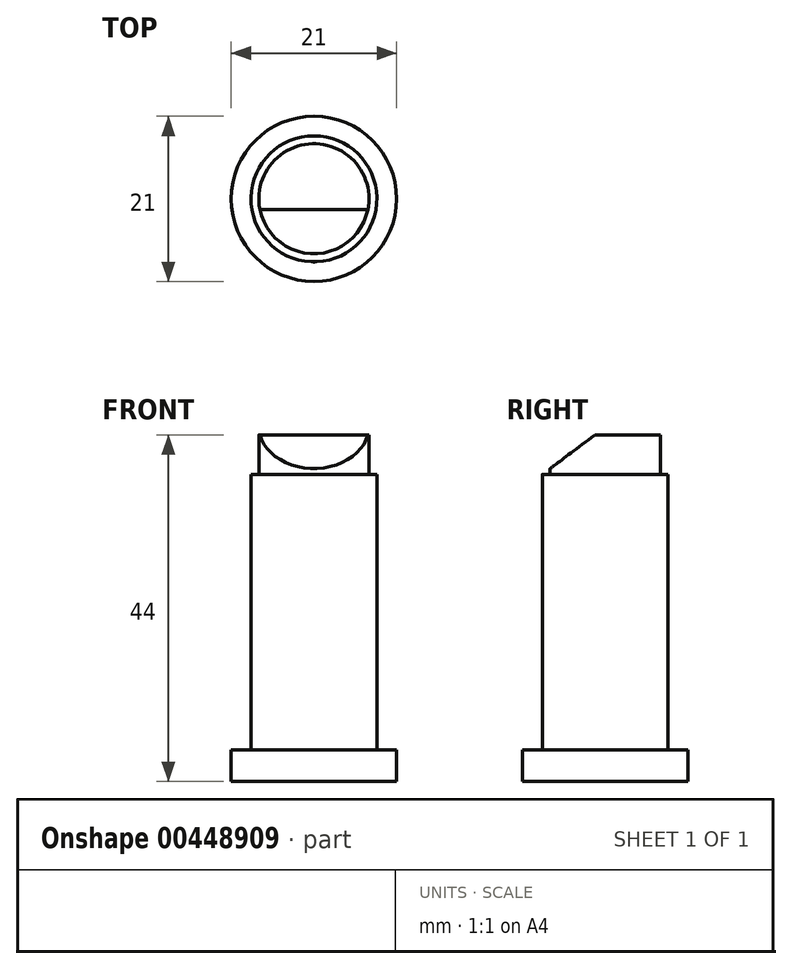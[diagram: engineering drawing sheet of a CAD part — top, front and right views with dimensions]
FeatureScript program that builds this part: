
annotation { "Feature Type Name" : "Feature", "Feature Type Description" : "" }
export const myFeature = defineFeature(function(context is Context, id is Id, definition is map)
    precondition{}
    {
        {
            var Q0;
            Q0=qCreatedBy(makeId("Top.planeOp"),FACE);
            var sketch = newSketch(context, id + "F0", { "sketchPlane" : qUnion([Q0])});
            skCircle(sketch, "E0", {"center": v(0, 0) * mm, "radius": 10.5 * mm});
            skSolve(sketch);
        }
        {
            var Q0;
            Q0=qSketchRegion(id+"F0",true);
            extrude(context, id + "F1", {"entities" : qUnion([Q0]), "depth" : 4 * mm});
        }
        {
            var Q0;
            Q0=qCreatedBy(makeId("Top.planeOp"),FACE);
            var sketch = newSketch(context, id + "F2", { "sketchPlane" : qUnion([Q0])});
            skCircle(sketch, "E1", {"center": v(0, 0) * mm, "radius": 8 * mm});
            skSolve(sketch);
        }
        {
            var Q0;
            Q0=qSketchRegion(id+"F2",true);
            extrude(context, id + "F3", {"entities" : qUnion([Q0]), "operationType" : NewBodyOperationType.ADD, "depth" : 39 * mm});
        }
        {
            var Q0;
            Q0=qCreatedBy(makeId("Right.planeOp"),FACE);
            var sketch = newSketch(context, id + "F4", { "sketchPlane" : qUnion([Q0])});
            skLineSegment(sketch, "E2", {"start": v(0, 44) * mm, "end": v(0, 39) * mm});
            skLineSegment(sketch, "E3", {"start": v(0, 39) * mm, "end": v(7, 39) * mm});
            skLineSegment(sketch, "E4", {"start": v(7, 39) * mm, "end": v(7, 44) * mm});
            skLineSegment(sketch, "E5", {"start": v(7, 44) * mm, "end": v(0, 44) * mm});
            skSolve(sketch);
        }
        {
            var Q0;
            Q0=makeQuery(id+"F4.imprint","IMPRINT",FACE,{"disambiguationData":[TD([[makeQuery(id+"F4.imprint","IMPRINT",EDGE,{"derivedFrom":sQuery(id+"F4.wireOp",EDGE,"E2")}),1.0]])]});
            var Q1;
            Q1=sQuery(id+"F4.wireOp",EDGE,"E2");
            revolve(context, id + "F5", {"operationType" : NewBodyOperationType.ADD, "entities" : qUnion([Q0]), "axis" : qUnion([Q1]), "revolveType" : RevolveType.FULL});
        }
        {
            var Q0;
            Q0=qCreatedBy(makeId("Right.planeOp"),FACE);
            var sketch = newSketch(context, id + "F6", { "sketchPlane" : qUnion([Q0])});
            skLineSegment(sketch, "E6", {"start": v(-8, 45) * mm, "end": v(-8, 39) * mm});
            skLineSegment(sketch, "E7", {"start": v(-8, 39) * mm, "end": v(0, 45) * mm});
            skLineSegment(sketch, "E8", {"start": v(0, 45) * mm, "end": v(-8, 45) * mm});
            skSolve(sketch);
        }
        {
            var Q0;
            Q0 = qSketchRegion(id + "F6", true);
            extrude(context, id + "F7", {"entities" : qUnion([Q0]), "operationType" : NewBodyOperationType.REMOVE, "depth" : 25 * mm, "hasSecondDirection" : true, "secondDirectionOppositeDirection" : true, "secondDirectionDepth" : 25 * mm});
        }
    });
